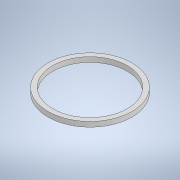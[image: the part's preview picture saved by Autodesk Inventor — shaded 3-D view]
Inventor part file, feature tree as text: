
AUTODESK INVENTOR PART (.ipt)
format: ipt  version: 2020 (Build 240168000, 168)  size: 104,960 bytes
history: native  units: in
note: dims shown in document units (in); Inventor stores cm internally (conversion verified against a paired STEP export)
features: extrude x2, sketch x2
ambient origin geometry x8: Origin, YZ Plane, XZ Plane, XY Plane, X Axis, Y Axis, Z Axis, Center Point
bodies: Solid1 (feature_tree)
feature tree (4):
  extrude  "Extrusion1"  Depth=0.1in TaperAngle=0.0deg
  extrude  "Extrusion2"  Depth=0.2in TaperAngle=0.0deg
  sketch  "Sketch1"  dims[d0=1.7in d1=0.1in d2=0.0in]
  sketch  "Sketch2"  dims[d3=1.51in d4=0.2in d5=0.0in]
